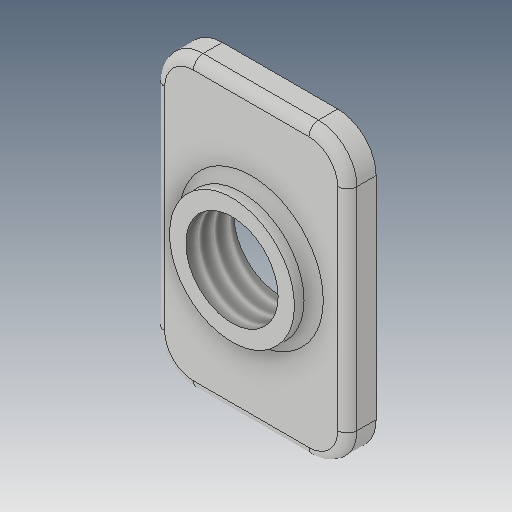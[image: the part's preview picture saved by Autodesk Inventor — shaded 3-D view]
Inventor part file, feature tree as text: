
AUTODESK INVENTOR PART (.ipt)
format: ipt  version: 2017 (Build 210142000, 142)  size: 178,176 bytes
history: native  units: mm
features: other x3, sketch x2
ambient origin geometry x8: Origin, YZ Plane, XZ Plane, XY Plane, X Axis, Y Axis, Z Axis, Center Point
bodies: Solid1 (feature_tree)
feature tree (5):
  other  "M5 Tee Nut-Generic_MIR_CPY_CPY.ipt"
  other  "Solid1::M5 Tee Nut-Generic_MIR_CPY_CPY.ipt"
  other  "TaggingFeature1"
  sketch  "Sketch1"  dims[d0=10.0mm]
  sketch  "Sketch2"
